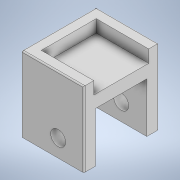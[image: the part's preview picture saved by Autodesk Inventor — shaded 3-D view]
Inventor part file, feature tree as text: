
AUTODESK INVENTOR PART (.ipt)
format: ipt  version: 2021.4 (Build 254397000, 397)  size: 163,840 bytes
history: native  units: mm
features: sketch x6, extrude x5, other x1, hole x1, fillet x1
ambient origin geometry x8: Origin, YZ Plane, XZ Plane, XY Plane, X Axis, Y Axis, Z Axis, Center Point
bodies: Body1 (feature_tree)
feature tree (14):
  other  "ソリッド1"
  extrude  "押し出し1"  Depth=25.0mm
  extrude  "押し出し2"  Depth=30.0mm
  hole  "穴1"  [1 undecoded]
  extrude  "押し出し4"  Depth=20.5mm
  extrude  "押し出し5"  Depth=20.5mm
  extrude  "押し出し6"  Depth=20.0mm TaperAngle=0.0deg
  fillet  "フィレット2"  Radius=7.0mm
  sketch  "スケッチ1"
  sketch  "スケッチ2"
  sketch  "スケッチ4"
  sketch  "スケッチ5"
  sketch  "スケッチ6"
  sketch  "スケッチ7"
note: 1 required parameter value undecoded (feature->parameter linkage not recoverable at this tier; creation-order binding heuristic only, values carry confidence <= 0.55)
